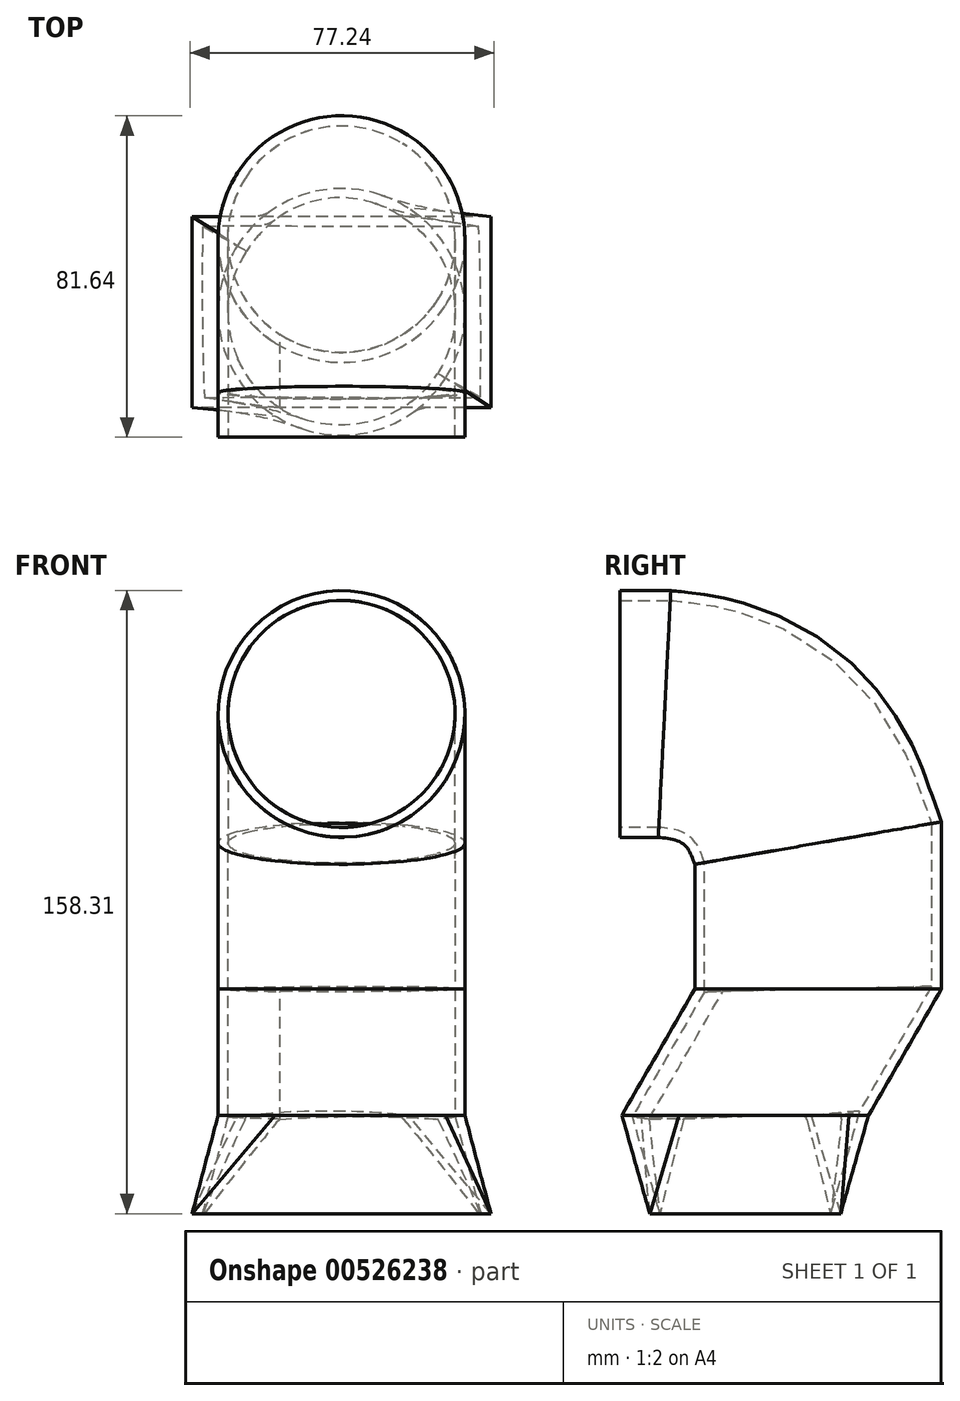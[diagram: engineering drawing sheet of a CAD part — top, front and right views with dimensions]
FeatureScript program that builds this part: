
annotation { "Feature Type Name" : "Feature", "Feature Type Description" : "" }
export const myFeature = defineFeature(function(context is Context, id is Id, definition is map)
    precondition{}
    {
        {
            var Q0;
            Q0=qCreatedBy(makeId("Top.planeOp"),FACE);
            var sketch = newSketch(context, id + "F0", { "sketchPlane" : qUnion([Q0])});
            skLineSegment(sketch, "E0.bottom", {"start": v(37.97, -24.25) * mm, "end": v(-37.97, -24.25) * mm});
            skLineSegment(sketch, "E0.top", {"start": v(37.97, 24.25) * mm, "end": v(-37.97, 24.25) * mm});
            skLineSegment(sketch, "E0.left", {"start": v(37.97, -24.25) * mm, "end": v(37.97, 24.25) * mm});
            skLineSegment(sketch, "E0.right", {"start": v(-37.97, -24.25) * mm, "end": v(-37.97, 24.25) * mm});
            skPoint(sketch, "E0.middle", {"position": v(0, 0) * mm});
            skSolve(sketch);
        }
        {
            var Q0;
            Q0=qCreatedBy(makeId("Top.planeOp"),FACE);
            cPlane(context, id + "F1", {"entities" : qUnion([Q0]), "cplaneType" : CPlaneType.OFFSET, "offset" : 25 * mm, "width" : 150 * mm, "height" : 150 * mm});
        }
        {
            var Q0;
            Q0=qCreatedBy(id+"F1.planeOp",FACE);
            var sketch = newSketch(context, id + "F2", { "sketchPlane" : qUnion([Q0])});
            skCircle(sketch, "E1", {"center": v(0, 0) * mm, "radius": 31.33 * mm});
            skSolve(sketch);
        }
        {
            var Q0;
            Q0=makeQuery(id+"F0.imprint","IMPRINT",FACE,{"disambiguationData":[TD([[makeQuery(id+"F0.imprint","IMPRINT",EDGE,{"derivedFrom":sQuery(id+"F0.wireOp",EDGE,"E0.bottom")}),-1.0]])]});
            var Q1;
            Q1=makeQuery(id+"F2.imprint","IMPRINT",FACE,{"disambiguationData":[TD([[makeQuery(id+"F2.imprint","IMPRINT",EDGE,{"derivedFrom":sQuery(id+"F2.wireOp",EDGE,"E1")}),1.0]])]});
            loft(context, id + "F3", {"sheetProfilesArray" : [{ "sheetProfileEntities" : qUnion([Q0]) }, { "sheetProfileEntities" : qUnion([Q1]) }]});
        }
        {
            var Q0;
            Q0=qCreatedBy(makeId("Right.planeOp"),FACE);
            var sketch = newSketch(context, id + "F4", { "sketchPlane" : qUnion([Q0])});
            skLineSegment(sketch, "E2", {"start": v(-31.13, 25.03) * mm, "end": v(-12.62, 57.08) * mm});
            skSolve(sketch);
        }
        {
            var Q0;
            Q0=makeQuery(id+"F3.opLoft","CAP_FACE",FACE,{"disambiguationData":[OSD([makeQuery(id+"F2.imprint","IMPRINT",FACE,{"disambiguationData":[TD([[makeQuery(id+"F2.imprint","IMPRINT",EDGE,{"derivedFrom":sQuery(id+"F2.wireOp",EDGE,"E1")}),1.0]])]})])],"isStart":true});
            var Q1;
            Q1=sQuery(id+"F4.wireOp",EDGE,"E2");
            sweep(context, id + "F5", {"operationType" : NewBodyOperationType.ADD, "profiles" : qUnion([Q0]), "path" : qUnion([Q1])});
        }
        {
            var Q0;
            Q0=qCreatedBy(makeId("Right.planeOp"),FACE);
            var sketch = newSketch(context, id + "F6", { "sketchPlane" : qUnion([Q0])});
            skLineSegment(sketch, "E3", {"start": v(-12.72, 57.05) * mm, "end": v(-12.72, 88.78) * mm});
            skFitSpline(sketch, "E4", {"points": [v(-12.72, 88.78) * mm, v(-15.66, 94.02) * mm, v(-22.09, 95.74) * mm], "startDerivative": vector(-4.45, 12.56) * mm, "endDerivative": vector(-14.2, 1.45) * mm});
            skLineSegment(sketch, "E5", {"start": v(-22.09, 95.74) * mm, "end": v(-31.8, 95.74) * mm});
            skSolve(sketch);
        }
        {
            var Q0;
            Q0=makeQuery(id+"F5.opSweep","CAP_FACE",FACE,{"disambiguationData":[OSD([makeQuery(id+"F2.imprint","IMPRINT",FACE,{"disambiguationData":[TD([[makeQuery(id+"F2.imprint","IMPRINT",EDGE,{"derivedFrom":sQuery(id+"F2.wireOp",EDGE,"E1")}),1.0]])]}),sQuery(id+"F4.wireOp",VERTEX,"E2.end")])],"isStart":false});
            var Q1;
            Q1=sQuery(id+"F6.wireOp",EDGE,"E3");
            var Q2;
            Q2=sQuery(id+"F6.wireOp",EDGE,"E4");
            var Q3;
            Q3=sQuery(id+"F6.wireOp",EDGE,"E5");
            sweep(context, id + "F7", {"operationType" : NewBodyOperationType.ADD, "profiles" : qUnion([Q0]), "path" : qUnion([Q1, Q2, Q3])});
        }
        {
            var Q0;
            Q0=makeQuery(id+"F7.opSweep","CAP_FACE",FACE,{"disambiguationData":[OSD([makeQuery(id+"F2.imprint","IMPRINT",FACE,{"disambiguationData":[TD([[makeQuery(id+"F2.imprint","IMPRINT",EDGE,{"derivedFrom":sQuery(id+"F2.wireOp",EDGE,"E1")}),1.0]])]}),sQuery(id+"F4.wireOp",VERTEX,"E2.end"),sQuery(id+"F6.wireOp",VERTEX,"E5.end")])],"isStart":false});
            var Q1;
            Q1=makeQuery(id+"F3.opLoft","CAP_FACE",FACE,{"disambiguationData":[OSD([makeQuery(id+"F0.imprint","IMPRINT",FACE,{"disambiguationData":[TD([[makeQuery(id+"F0.imprint","IMPRINT",EDGE,{"derivedFrom":sQuery(id+"F0.wireOp",EDGE,"E0.bottom")}),-1.0]])]})])],"isStart":true});
            shell(context, id + "F8", {"entities" : qUnion([Q0, Q1]), "thickness" : 2.5 * mm});
        }
    });
